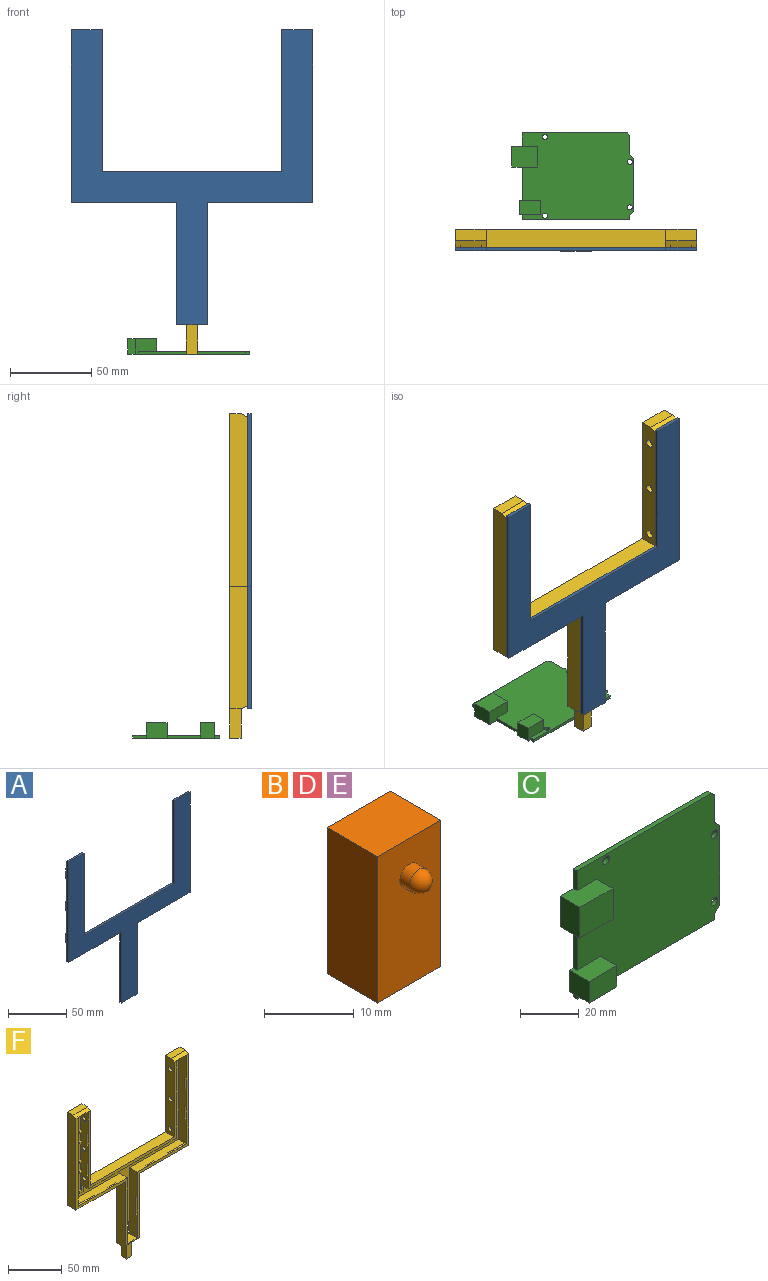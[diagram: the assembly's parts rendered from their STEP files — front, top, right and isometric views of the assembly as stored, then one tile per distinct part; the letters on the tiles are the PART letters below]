
ASSEMBLY  parts=6 mates=3
PART A: 170 faces, bbox 148x7x181 mm
  f0: plane 181x148mm, normal (0,1,0), area 6824.8mm2, adj f1,f2,f3,f4,f5,f6,f7,f11
  f1: plane 19x2mm, normal (0,0,-1), area 38mm2, adj f0,f7,f8,f84
  f2: plane 110x2mm, normal (0,0,1), area 220mm2, adj f0,f3,f8,f80
  f3: plane 87x2mm, normal (1,0,0), area 174mm2, adj f0,f2,f4,f8
  f4: plane 19x2mm, normal (0,0,1), area 38mm2, adj f0,f3,f5,f8
  f5: plane 106x2mm, normal (-1,0,0), area 212mm2, adj f0,f4,f6,f8
  f6: plane 64.5x2mm, normal (0,0,-1), area 129mm2, adj f0,f5,f7,f8
  f7: plane 75x2mm, normal (-1,0,0), area 150mm2, adj f0,f1,f6,f8
  f8: plane 181x148mm, normal (0,-1,0), area 7543mm2, adj f1,f2,f3,f4,f5,f6,f7,f80
  f9: plane 11.93x0.86mm, normal (0.71,0.71,0), area 14.2mm2, adj f10,f13,f14,f15
  f10: plane 13x2mm, normal (0,1,0), area 24.9mm2, adj f9,f11,f14,f15
  f11: plane 13x1.86mm, normal (-1,0,0), area 24.2mm2, adj f0,f10,f14,f15
  f12: plane 11.93x0.14mm, normal (1,0,0), area 1.7mm2, adj f0,f13,f14,f15
  f13: plane 11.93x0.86mm, normal (0.71,-0.71,0), area 14.2mm2, adj f9,f12,f14,f15
  f14: plane 2.86x1.86mm, normal (0.26,0,-0.97), area 4.6mm2, adj f0,f9,f10,f11,f12,f13
  f15: plane 2.86x1.86mm, normal (0.26,0,0.97), area 4.6mm2, adj f0,f9,f10,f11,f12,f13
  f16: plane 11.93x0.86mm, normal (-0.71,-0.71,0), area 14.2mm2, adj f17,f20,f21,f22
  f17: plane 11.93x0.14mm, normal (-1,0,0), area 1.7mm2, adj f0,f16,f21,f22
  f18: plane 13x1.86mm, normal (1,0,0), area 24.2mm2, adj f0,f19,f21,f22
  f19: plane 13x2mm, normal (0,1,0), area 24.9mm2, adj f18,f20,f21,f22
  f20: plane 11.93x0.86mm, normal (-0.71,0.71,0), area 14.2mm2, adj f16,f19,f21,f22
  f21: plane 2.86x1.86mm, normal (-0.26,0,-0.97), area 4.6mm2, adj f0,f16,f17,f18,f19,f20
  f22: plane 2.86x1.86mm, normal (-0.26,0,0.97), area 4.6mm2, adj f0,f16,f17,f18,f19,f20
  f23: plane 11.93x0.86mm, normal (0.71,0.71,0), area 14.2mm2, adj f24,f27,f28,f29
  f24: plane 13x2mm, normal (0,1,0), area 24.9mm2, adj f23,f25,f28,f29
  f25: plane 13x1.86mm, normal (-1,0,0), area 24.2mm2, adj f0,f24,f28,f29
  f26: plane 11.93x0.14mm, normal (1,0,0), area 1.7mm2, adj f0,f27,f28,f29
  f27: plane 11.93x0.86mm, normal (0.71,-0.71,0), area 14.2mm2, adj f23,f26,f28,f29
  f28: plane 2.86x1.86mm, normal (0.26,0,-0.97), area 4.6mm2, adj f0,f23,f24,f25,f26,f27
  f29: plane 2.86x1.86mm, normal (0.26,0,0.97), area 4.6mm2, adj f0,f23,f24,f25,f26,f27
  f30: plane 11.93x0.86mm, normal (-0.71,-0.71,0), area 14.2mm2, adj f31,f34,f35,f36
  f31: plane 11.93x0.14mm, normal (-1,0,0), area 1.7mm2, adj f0,f30,f35,f36
  f32: plane 13x1.86mm, normal (1,0,0), area 24.2mm2, adj f0,f33,f35,f36
  f33: plane 13x2mm, normal (0,1,0), area 24.9mm2, adj f32,f34,f35,f36
  f34: plane 11.93x0.86mm, normal (-0.71,0.71,0), area 14.2mm2, adj f30,f33,f35,f36
  f35: plane 2.86x1.86mm, normal (-0.26,0,-0.97), area 4.6mm2, adj f0,f30,f31,f32,f33,f34
  f36: plane 2.86x1.86mm, normal (-0.26,0,0.97), area 4.6mm2, adj f0,f30,f31,f32,f33,f34
  f37: plane 8.93x0.86mm, normal (0,-0.71,0.71), area 10.6mm2, adj f38,f41,f42,f43
  f38: plane 8.93x0.14mm, normal (0,0,1), area 1.3mm2, adj f0,f37,f42,f43
  f39: plane 10x1.86mm, normal (0,0,-1), area 18.6mm2, adj f0,f40,f42,f43
  f40: plane 10x2mm, normal (0,1,0), area 18.9mm2, adj f39,f41,f42,f43
  f41: plane 8.93x0.86mm, normal (0,0.71,0.71), area 10.6mm2, adj f37,f40,f42,f43
  f42: plane 2.86x1.86mm, normal (0.97,0,0.26), area 4.6mm2, adj f0,f37,f38,f39,f40,f41
  f43: plane 2.86x1.86mm, normal (-0.97,0,0.26), area 4.6mm2, adj f0,f37,f38,f39,f40,f41
  f44: plane 8.93x0.86mm, normal (0,-0.71,-0.71), area 10.6mm2, adj f45,f48,f49,f50
  f45: plane 8.93x0.86mm, normal (0,0.71,-0.71), area 10.6mm2, adj f44,f46,f49,f50
  f46: plane 10x2mm, normal (0,1,0), area 18.9mm2, adj f45,f47,f49,f50
  f47: plane 10x1.86mm, normal (0,0,1), area 18.6mm2, adj f0,f46,f49,f50
  f48: plane 8.93x0.14mm, normal (0,0,-1), area 1.3mm2, adj f0,f44,f49,f50
  f49: plane 2.86x1.86mm, normal (0.97,0,-0.26), area 4.6mm2, adj f0,f44,f45,f46,f47,f48
  f50: plane 2.86x1.86mm, normal (-0.97,0,-0.26), area 4.6mm2, adj f0,f44,f45,f46,f47,f48
  f51: plane 2.86x1.86mm, normal (-0.97,0,0.26), area 4.6mm2, adj f0,f52,f53,f54,f55
  f52: plane 9x1mm, normal (0,-0.71,0.71), area 12.4mm2, adj f0,f51,f53,f56
  f53: plane 8.93x0.86mm, normal (0,0.71,0.71), area 10.6mm2, adj f51,f52,f54,f56
  f54: plane 10x2mm, normal (0,1,0), area 18.9mm2, adj f51,f53,f55,f56
  f55: plane 10x1.86mm, normal (0,0,-1), area 18.6mm2, adj f0,f51,f54,f56
  f56: plane 2.86x1.86mm, normal (0.97,0,0.26), area 4.6mm2, adj f0,f52,f53,f54,f55
  f57: plane 21.93x1.86mm, normal (0,0,-1), area 40.8mm2, adj f0,f59,f60,f61
  f58: plane 23x1.86mm, normal (0,0,1), area 42.7mm2, adj f0,f59,f60,f61
  f59: plane 23x2mm, normal (0,1,0), area 44.9mm2, adj f57,f58,f60,f61
  f60: plane 2x1.86mm, normal (0.97,0,-0.26), area 3.8mm2, adj f0,f57,f58,f59
  f61: plane 2x1.86mm, normal (-0.97,0,-0.26), area 3.8mm2, adj f0,f57,f58,f59
  f62: plane 5x4mm, normal (0,0,1), area 16.9mm2, adj f0,f63,f65,f66,f77
  f63: plane 10x2.5mm, normal (1,0,0), area 25mm2, adj f0,f62,f64,f77
  f64: plane 5x4mm, normal (0,0,-1), area 16.9mm2, adj f0,f63,f65,f66,f77
  f65: plane 10x5mm, normal (-1,0,0), area 50mm2, adj f0,f62,f64,f66
  f66: plane 10x1.5mm, normal (0,1,0), area 15mm2, adj f62,f64,f65,f77
  f67: plane 5x4mm, normal (0,0,1), area 16.9mm2, adj f0,f68,f70,f71,f78
  f68: plane 10x2.5mm, normal (1,0,0), area 25mm2, adj f0,f67,f69,f78
  f69: plane 5x4mm, normal (0,0,-1), area 16.9mm2, adj f0,f68,f70,f71,f78
  f70: plane 10x5mm, normal (-1,0,0), area 50mm2, adj f0,f67,f69,f71
  f71: plane 10x1.5mm, normal (0,1,0), area 15mm2, adj f67,f69,f70,f78
  f72: plane 5x4mm, normal (0,0,1), area 16.9mm2, adj f0,f73,f75,f76,f79
  f73: plane 10x2.5mm, normal (1,0,0), area 25mm2, adj f0,f72,f74,f79
  f74: plane 5x4mm, normal (0,0,-1), area 16.9mm2, adj f0,f73,f75,f76,f79
  f75: plane 10x5mm, normal (-1,0,0), area 50mm2, adj f0,f72,f74,f76
  f76: plane 10x1.5mm, normal (0,1,0), area 15mm2, adj f72,f74,f75,f79
  f77: plane 10x2.5mm, normal (0.71,0.71,0), area 35.4mm2, adj f62,f63,f64,f66
  f78: plane 10x2.5mm, normal (0.71,0.71,0), area 35.4mm2, adj f67,f68,f69,f71
  f79: plane 10x2.5mm, normal (0.71,0.71,0), area 35.4mm2, adj f72,f73,f74,f76
  f80: plane 87x2mm, normal (-1,0,0), area 174mm2, adj f0,f2,f8,f81
  f81: plane 19x2mm, normal (0,0,1), area 38mm2, adj f0,f8,f80,f82
  f82: plane 106x2mm, normal (1,0,0), area 212mm2, adj f0,f8,f81,f83
  f83: plane 64.5x2mm, normal (0,0,-1), area 129mm2, adj f0,f8,f82,f84
  f84: plane 75x2mm, normal (1,0,0), area 150mm2, adj f0,f1,f8,f83
  f85: plane 11.93x0.86mm, normal (-0.71,0.71,0), area 14.2mm2, adj f86,f89,f90,f91
  f86: plane 13x2mm, normal (0,1,0), area 24.9mm2, adj f85,f87,f90,f91
  f87: plane 13x1.86mm, normal (1,0,0), area 24.2mm2, adj f0,f86,f90,f91
  f88: plane 11.93x0.14mm, normal (-1,0,0), area 1.7mm2, adj f0,f89,f90,f91
  f89: plane 11.93x0.86mm, normal (-0.71,-0.71,0), area 14.2mm2, adj f85,f88,f90,f91
  f90: plane 2.86x1.86mm, normal (-0.26,0,-0.97), area 4.6mm2, adj f0,f85,f86,f87,f88,f89
  f91: plane 2.86x1.86mm, normal (-0.26,0,0.97), area 4.6mm2, adj f0,f85,f86,f87,f88,f89
  f92: plane 11.93x0.86mm, normal (0.71,-0.71,0), area 14.2mm2, adj f93,f96,f97,f98
  f93: plane 11.93x0.14mm, normal (1,0,0), area 1.7mm2, adj f0,f92,f97,f98
  f94: plane 13x1.86mm, normal (-1,0,0), area 24.2mm2, adj f0,f95,f97,f98
  f95: plane 13x2mm, normal (0,1,0), area 24.9mm2, adj f94,f96,f97,f98
  f96: plane 11.93x0.86mm, normal (0.71,0.71,0), area 14.2mm2, adj f92,f95,f97,f98
  f97: plane 2.86x1.86mm, normal (0.26,0,-0.97), area 4.6mm2, adj f0,f92,f93,f94,f95,f96
  f98: plane 2.86x1.86mm, normal (0.26,0,0.97), area 4.6mm2, adj f0,f92,f93,f94,f95,f96
  f99: plane 11.93x0.86mm, normal (-0.71,0.71,0), area 14.2mm2, adj f100,f103,f104,f105
  f100: plane 13x2mm, normal (0,1,0), area 24.9mm2, adj f99,f101,f104,f105
  f101: plane 13x1.86mm, normal (1,0,0), area 24.2mm2, adj f0,f100,f104,f105
  f102: plane 11.93x0.14mm, normal (-1,0,0), area 1.7mm2, adj f0,f103,f104,f105
  f103: plane 11.93x0.86mm, normal (-0.71,-0.71,0), area 14.2mm2, adj f99,f102,f104,f105
  f104: plane 2.86x1.86mm, normal (-0.26,0,-0.97), area 4.6mm2, adj f0,f99,f100,f101,f102,f103
  f105: plane 2.86x1.86mm, normal (-0.26,0,0.97), area 4.6mm2, adj f0,f99,f100,f101,f102,f103
  f106: plane 11.93x0.86mm, normal (0.71,-0.71,0), area 14.2mm2, adj f107,f110,f111,f112
  f107: plane 11.93x0.14mm, normal (1,0,0), area 1.7mm2, adj f0,f106,f111,f112
  f108: plane 13x1.86mm, normal (-1,0,0), area 24.2mm2, adj f0,f109,f111,f112
  f109: plane 13x2mm, normal (0,1,0), area 24.9mm2, adj f108,f110,f111,f112
  f110: plane 11.93x0.86mm, normal (0.71,0.71,0), area 14.2mm2, adj f106,f109,f111,f112
  f111: plane 2.86x1.86mm, normal (0.26,0,-0.97), area 4.6mm2, adj f0,f106,f107,f108,f109,f110
  f112: plane 2.86x1.86mm, normal (0.26,0,0.97), area 4.6mm2, adj f0,f106,f107,f108,f109,f110
  f113: plane 8.93x0.86mm, normal (0,-0.71,0.71), area 10.6mm2, adj f114,f117,f118,f119
  f114: plane 8.93x0.14mm, normal (0,0,1), area 1.3mm2, adj f0,f113,f118,f119
  f115: plane 10x1.86mm, normal (0,0,-1), area 18.6mm2, adj f0,f116,f118,f119
  f116: plane 10x2mm, normal (0,1,0), area 18.9mm2, adj f115,f117,f118,f119
  f117: plane 8.93x0.86mm, normal (0,0.71,0.71), area 10.6mm2, adj f113,f116,f118,f119
  f118: plane 2.86x1.86mm, normal (-0.97,0,0.26), area 4.6mm2, adj f0,f113,f114,f115,f116,f117
  f119: plane 2.86x1.86mm, normal (0.97,0,0.26), area 4.6mm2, adj f0,f113,f114,f115,f116,f117
  f120: plane 8.93x0.86mm, normal (0,-0.71,-0.71), area 10.6mm2, adj f121,f124,f125,f126
  f121: plane 8.93x0.86mm, normal (0,0.71,-0.71), area 10.6mm2, adj f120,f122,f125,f126
  f122: plane 10x2mm, normal (0,1,0), area 18.9mm2, adj f121,f123,f125,f126
  f123: plane 10x1.86mm, normal (0,0,1), area 18.6mm2, adj f0,f122,f125,f126
  f124: plane 8.93x0.14mm, normal (0,0,-1), area 1.3mm2, adj f0,f120,f125,f126
  f125: plane 2.86x1.86mm, normal (-0.97,0,-0.26), area 4.6mm2, adj f0,f120,f121,f122,f123,f124
  f126: plane 2.86x1.86mm, normal (0.97,0,-0.26), area 4.6mm2, adj f0,f120,f121,f122,f123,f124
  f127: plane 2.86x1.86mm, normal (0.97,0,0.26), area 4.6mm2, adj f0,f128,f129,f130,f131
  f128: plane 9x1mm, normal (0,-0.71,0.71), area 12.4mm2, adj f0,f127,f129,f132
  f129: plane 8.93x0.86mm, normal (0,0.71,0.71), area 10.6mm2, adj f127,f128,f130,f132
  f130: plane 10x2mm, normal (0,1,0), area 18.9mm2, adj f127,f129,f131,f132
  f131: plane 10x1.86mm, normal (0,0,-1), area 18.6mm2, adj f0,f127,f130,f132
  f132: plane 2.86x1.86mm, normal (-0.97,0,0.26), area 4.6mm2, adj f0,f128,f129,f130,f131
  f133: plane 21.93x1.86mm, normal (0,0,-1), area 40.8mm2, adj f0,f135,f136,f137
  f134: plane 23x1.86mm, normal (0,0,1), area 42.7mm2, adj f0,f135,f136,f137
  f135: plane 23x2mm, normal (0,1,0), area 44.9mm2, adj f133,f134,f136,f137
  f136: plane 2x1.86mm, normal (-0.97,0,-0.26), area 3.8mm2, adj f0,f133,f134,f135
  f137: plane 2x1.86mm, normal (0.97,0,-0.26), area 3.8mm2, adj f0,f133,f134,f135
  f138: plane 5x4mm, normal (0,0,1), area 16.9mm2, adj f0,f139,f141,f142,f153
  f139: plane 10x2.5mm, normal (-1,0,0), area 25mm2, adj f0,f138,f140,f153
  f140: plane 5x4mm, normal (0,0,-1), area 16.9mm2, adj f0,f139,f141,f142,f153
  f141: plane 10x5mm, normal (1,0,0), area 50mm2, adj f0,f138,f140,f142
  f142: plane 10x1.5mm, normal (0,1,0), area 15mm2, adj f138,f140,f141,f153
  f143: plane 5x4mm, normal (0,0,1), area 16.9mm2, adj f0,f144,f146,f147,f154
  f144: plane 10x2.5mm, normal (-1,0,0), area 25mm2, adj f0,f143,f145,f154
  f145: plane 5x4mm, normal (0,0,-1), area 16.9mm2, adj f0,f144,f146,f147,f154
  f146: plane 10x5mm, normal (1,0,0), area 50mm2, adj f0,f143,f145,f147
  f147: plane 10x1.5mm, normal (0,1,0), area 15mm2, adj f143,f145,f146,f154
  f148: plane 5x4mm, normal (0,0,1), area 16.9mm2, adj f0,f149,f151,f152,f155
  f149: plane 10x2.5mm, normal (-1,0,0), area 25mm2, adj f0,f148,f150,f155
  f150: plane 5x4mm, normal (0,0,-1), area 16.9mm2, adj f0,f149,f151,f152,f155
  f151: plane 10x5mm, normal (1,0,0), area 50mm2, adj f0,f148,f150,f152
  f152: plane 10x1.5mm, normal (0,1,0), area 15mm2, adj f148,f150,f151,f155
  f153: plane 10x2.5mm, normal (-0.71,0.71,0), area 35.4mm2, adj f138,f139,f140,f142
  f154: plane 10x2.5mm, normal (-0.71,0.71,0), area 35.4mm2, adj f143,f144,f145,f147
  f155: plane 10x2.5mm, normal (-0.71,0.71,0), area 35.4mm2, adj f148,f149,f150,f152
  f156: plane 18.93x0.86mm, normal (-0.71,-0.71,0), area 22.7mm2, adj f157,f160,f161,f162
  f157: plane 18.93x0.14mm, normal (-1,0,0), area 2.7mm2, adj f0,f156,f161,f162
  f158: plane 20x1.86mm, normal (1,0,0), area 37.2mm2, adj f0,f159,f161,f162
  f159: plane 20x2mm, normal (0,1,0), area 38.9mm2, adj f158,f160,f161,f162
  f160: plane 18.93x0.86mm, normal (-0.71,0.71,0), area 22.7mm2, adj f156,f159,f161,f162
  f161: plane 2.86x1.86mm, normal (-0.26,0,0.97), area 4.6mm2, adj f0,f156,f157,f158,f159,f160
  f162: plane 2.86x1.86mm, normal (-0.26,0,-0.97), area 4.6mm2, adj f0,f156,f157,f158,f159,f160
  f163: plane 18.93x0.86mm, normal (0.71,0.71,0), area 22.7mm2, adj f164,f167,f168,f169
  f164: plane 20x2mm, normal (0,1,0), area 38.9mm2, adj f163,f165,f168,f169
  f165: plane 20x1.86mm, normal (-1,0,0), area 37.2mm2, adj f0,f164,f168,f169
  f166: plane 18.93x0.14mm, normal (1,0,0), area 2.7mm2, adj f0,f167,f168,f169
  f167: plane 18.93x0.86mm, normal (0.71,-0.71,0), area 22.7mm2, adj f163,f166,f168,f169
  f168: plane 2.86x1.86mm, normal (0.26,0,0.97), area 4.6mm2, adj f0,f163,f164,f165,f166,f167
  f169: plane 2.86x1.86mm, normal (0.26,0,-0.97), area 4.6mm2, adj f0,f163,f164,f165,f166,f167
PART B: 8 faces, bbox 10x11x20 mm
  f0: plane 10x8mm, normal (0,0,1), area 80mm2, adj f1,f3,f4,f5
  f1: plane 20x8mm, normal (-1,0,0), area 160mm2, adj f0,f2,f4,f5
  f2: plane 10x8mm, normal (0,0,-1), area 80mm2, adj f1,f3,f4,f5
  f3: plane 20x8mm, normal (1,0,0), area 160mm2, adj f0,f2,f4,f5
  f4: plane 20x10mm, normal (0,-1,0), area 192.9mm2, adj f0,f1,f2,f3,f6
  f5: plane 20x10mm, normal (0,1,0), area 200mm2, adj f0,f1,f2,f3
  f6: cylinder r=1.5mm len=3mm, axis (0,1,0), area 14.1mm2, adj f4,f7
  f7: sphere r=1.5mm, area 14.1mm2, adj f6
PART C: 27 faces, bbox 74.9x9.5x53.3 mm
  f0: plane 20.32x1.78mm, normal (-1,0,0), area 36.1mm2, adj f3,f16,f17,f23
  f1: plane 3.18x1.78mm, normal (-1,0,0), area 5.6mm2, adj f3,f6,f16,f22
  f2: plane 8.26x1.78mm, normal (-1,0,0), area 14.7mm2, adj f3,f5,f16,f18
  f3: plane 68.58x53.34mm, normal (0,-1,0), area 3356.8mm2, adj f0,f1,f2,f4,f5,f6,f7,f8
  f4: plane 1.78x1.52mm, normal (0.71,0,0.71), area 3.8mm2, adj f3,f5,f15,f16
  f5: plane 64.52x1.78mm, normal (0,0,1), area 114.7mm2, adj f2,f3,f4,f16
  f6: plane 66.04x1.78mm, normal (0,0,-1), area 117.4mm2, adj f1,f3,f7,f16
  f7: plane 2.54x1.78mm, normal (1,0,0), area 4.5mm2, adj f3,f6,f8,f16
  f8: plane 2.54x2.54mm, normal (0.71,0,-0.71), area 6.4mm2, adj f3,f7,f9,f16
  f9: plane 32.77x1.78mm, normal (1,0,0), area 58.3mm2, adj f3,f8,f10,f16
  f10: plane 2.54x2.54mm, normal (0.71,0,0.71), area 6.4mm2, adj f3,f9,f15,f16
  f11: cylinder r=1.59mm len=3.18mm, axis (0,1,0), area 17.7mm2, adj f3,f16
  f12: cylinder r=1.59mm len=3.18mm, axis (0,1,0), area 17.7mm2, adj f3,f16
  f13: cylinder r=1.59mm len=3.18mm, axis (0,1,0), area 17.7mm2, adj f3,f16
  f14: cylinder r=1.59mm len=3.18mm, axis (0,1,0), area 17.7mm2, adj f3,f16
  f15: plane 11.43x1.78mm, normal (1,0,0), area 20.3mm2, adj f3,f4,f10,f16
  f16: plane 74.93x53.34mm, normal (0,1,0), area 3677mm2, adj f0,f1,f2,f4,f5,f6,f7,f8
  f17: plane 15.88x9.53mm, normal (0,0,-1), area 134.3mm2, adj f0,f3,f16,f19,f20,f21
  f18: plane 15.88x9.53mm, normal (0,0,1), area 134.3mm2, adj f2,f3,f16,f19,f20,f21
  f19: plane 12.7x9.53mm, normal (-1,0,0), area 121mm2, adj f16,f17,f18,f21
  f20: plane 12.7x7.75mm, normal (1,0,0), area 98.4mm2, adj f3,f17,f18,f21
  f21: plane 15.88x12.7mm, normal (0,-1,0), area 201.6mm2, adj f17,f18,f19,f20
  f22: plane 13.34x9.53mm, normal (0,0,-1), area 106.7mm2, adj f1,f3,f16,f24,f25,f26
  f23: plane 13.34x9.53mm, normal (0,0,1), area 106.7mm2, adj f0,f3,f16,f24,f25,f26
  f24: plane 8.89x7.75mm, normal (1,0,0), area 68.9mm2, adj f3,f22,f23,f26
  f25: plane 9.53x8.89mm, normal (-1,0,0), area 84.7mm2, adj f16,f22,f23,f26
  f26: plane 13.34x8.89mm, normal (0,-1,0), area 118.5mm2, adj f22,f23,f24,f25
PART D: same geometry as B
PART E: same geometry as B
PART F: 152 faces, bbox 148x11.3x199 mm
  f0: plane 162x142mm, normal (0,-1,0), area 4853.4mm2, adj f2,f3,f4,f5,f6,f8,f10,f22
  f1: plane 177x148mm, normal (0,-1,0), area 1462mm2, adj f2,f3,f4,f6,f9,f14,f15,f16
  f2: plane 75x11.25mm, normal (1,0,0), area 742.7mm2, adj f0,f1,f4,f7,f9,f140,f142,f143
  f3: plane 75x11.25mm, normal (-1,0,0), area 742.7mm2, adj f0,f1,f7,f9,f73,f137,f138,f139
  f4: plane 64.5x10.25mm, normal (0,0,1), area 595.1mm2, adj f0,f1,f2,f6,f62,f64,f70,f71
  f5: plane 93.85x10.25mm, normal (-1,0,0), area 785.8mm2, adj f0,f8,f10,f18,f19,f20,f21,f22
  f6: plane 102x10.25mm, normal (1,0,0), area 984.2mm2, adj f0,f1,f4,f8,f44,f45,f46,f56
  f7: plane 199x148mm, normal (0,1,0), area 7488.3mm2, adj f2,f3,f9,f11,f12,f13,f14,f15
  f8: plane 13x10.25mm, normal (0,0,-1), area 133.2mm2, adj f0,f5,f6,f145
  f9: plane 13x11.25mm, normal (0,0,1), area 146.2mm2, adj f1,f2,f3,f7
  f10: plane 116x10.25mm, normal (0,0,-1), area 1103mm2, adj f0,f5,f18,f38,f42,f59,f61,f65
  f11: plane 110x11.25mm, normal (0,0,1), area 1237.5mm2, adj f7,f12,f18,f77
  f12: plane 87x11.25mm, normal (1,0,0), area 915.8mm2, adj f7,f11,f13,f18,f19,f20,f21,f145
  f13: plane 19x7.25mm, normal (0,0,1), area 137.7mm2, adj f7,f12,f14,f145
  f14: plane 106x11.25mm, normal (-1,0,0), area 1188.5mm2, adj f1,f7,f13,f15,f145
  f15: plane 64.5x11.25mm, normal (0,0,-1), area 725.6mm2, adj f1,f7,f14,f16
  f16: plane 75x11.25mm, normal (-1,0,0), area 839.8mm2, adj f1,f7,f15,f17,f146
  f17: plane 19x7.25mm, normal (0,0,-1), area 87.7mm2, adj f7,f16,f81,f146,f147,f148,f149
  f18: plane 116x88mm, normal (0,-1,0), area 858mm2, adj f5,f10,f11,f12,f48,f52,f60,f66
  f19: cylinder r=2.5mm len=5mm, axis (-1,0,0), area 47.1mm2, adj f5,f12
  f20: cylinder r=2.5mm len=5mm, axis (-1,0,0), area 47.1mm2, adj f5,f12
  f21: cylinder r=2.5mm len=5mm, axis (-1,0,0), area 47.1mm2, adj f5,f12
  f22: plane 2.5x2mm, normal (0,0,1), area 5mm2, adj f0,f5,f23,f25
  f23: plane 2x2mm, normal (-1,0,0), area 4mm2, adj f0,f22,f24,f25
  f24: plane 2.5x2mm, normal (0,0,-1), area 5mm2, adj f0,f5,f23,f25
  f25: plane 2.5x2mm, normal (0,-1,0), area 5mm2, adj f5,f22,f23,f24
  f26: plane 2.5x2mm, normal (0,0,1), area 5mm2, adj f0,f5,f27,f29
  f27: plane 2x2mm, normal (-1,0,0), area 4mm2, adj f0,f26,f28,f29
  f28: plane 2.5x2mm, normal (0,0,-1), area 5mm2, adj f0,f5,f27,f29
  f29: plane 2.5x2mm, normal (0,-1,0), area 5mm2, adj f5,f26,f27,f28
  f30: plane 2.5x2mm, normal (0,0,-1), area 5mm2, adj f0,f5,f32,f33
  f31: plane 2.5x2mm, normal (0,0,1), area 5mm2, adj f0,f5,f32,f33
  f32: plane 2x2mm, normal (-1,0,0), area 4mm2, adj f0,f30,f31,f33
  f33: plane 2.5x2mm, normal (0,-1,0), area 5mm2, adj f5,f30,f31,f32
  f34: plane 2.5x2mm, normal (0,0,-1), area 5mm2, adj f0,f5,f36,f37
  f35: plane 2.5x2mm, normal (0,0,1), area 5mm2, adj f0,f5,f36,f37
  f36: plane 2x2mm, normal (-1,0,0), area 4mm2, adj f0,f34,f35,f37
  f37: plane 2.5x2mm, normal (0,-1,0), area 5mm2, adj f5,f34,f35,f36
  f38: plane 7.85x2mm, normal (1,0,0), area 15.7mm2, adj f0,f10,f41,f42
  f39: plane 2.5x2mm, normal (0,0,1), area 5mm2, adj f0,f5,f40,f42
  f40: plane 2x2mm, normal (-1,0,0), area 4mm2, adj f0,f39,f41,f42
  f41: plane 4x2mm, normal (0,0,-1), area 8mm2, adj f0,f38,f40,f42
  f42: plane 7.85x4mm, normal (0,-1,0), area 16.8mm2, adj f5,f10,f38,f39,f40,f41
  f43: plane 13x1mm, normal (0.71,0.71,0), area 18.4mm2, adj f1,f44,f45,f46
  f44: plane 13x1mm, normal (0.71,-0.71,0), area 18.4mm2, adj f6,f43,f45,f46
  f45: plane 2x1mm, normal (0,0,1), area 1mm2, adj f6,f43,f44
  f46: plane 2x1mm, normal (0,0,-1), area 1mm2, adj f6,f43,f44
  f47: plane 13x1mm, normal (-0.71,-0.71,0), area 18.4mm2, adj f5,f48,f49,f50
  f48: plane 13x1mm, normal (-0.71,0.71,0), area 18.4mm2, adj f18,f47,f49,f50
  f49: plane 2x1mm, normal (0,0,1), area 1mm2, adj f5,f47,f48
  f50: plane 2x1mm, normal (0,0,-1), area 1mm2, adj f5,f47,f48
  f51: plane 13x1mm, normal (-0.71,-0.71,0), area 18.4mm2, adj f5,f52,f53,f54
  f52: plane 13x1mm, normal (-0.71,0.71,0), area 18.4mm2, adj f18,f51,f53,f54
  f53: plane 2x1mm, normal (0,0,1), area 1mm2, adj f5,f51,f52
  f54: plane 2x1mm, normal (0,0,-1), area 1mm2, adj f5,f51,f52
  f55: plane 13x1mm, normal (0.71,0.71,0), area 18.4mm2, adj f1,f56,f57,f58
  f56: plane 13x1mm, normal (0.71,-0.71,0), area 18.4mm2, adj f6,f55,f57,f58
  f57: plane 2x1mm, normal (0,0,1), area 1mm2, adj f6,f55,f56
  f58: plane 2x1mm, normal (0,0,-1), area 1mm2, adj f6,f55,f56
  f59: plane 10x1mm, normal (0,-0.71,-0.71), area 14.1mm2, adj f5,f10,f60,f61
  f60: plane 10x1mm, normal (0,0.71,-0.71), area 14.1mm2, adj f5,f18,f59,f61
  f61: plane 2x1mm, normal (-1,0,0), area 1mm2, adj f10,f59,f60
  f62: plane 2x1mm, normal (-1,0,0), area 1mm2, adj f4,f63,f64
  f63: plane 23x1mm, normal (0,0.71,0.71), area 32.5mm2, adj f1,f6,f62,f64
  f64: plane 23x1mm, normal (0,-0.71,0.71), area 32.5mm2, adj f4,f6,f62,f63
  f65: plane 10x1mm, normal (0,-0.71,-0.71), area 14.1mm2, adj f10,f66,f67,f68
  f66: plane 10x1mm, normal (0,0.71,-0.71), area 14.1mm2, adj f18,f65,f67,f68
  f67: plane 2x1mm, normal (-1,0,0), area 1mm2, adj f10,f65,f66
  f68: plane 2x1mm, normal (1,0,0), area 1mm2, adj f10,f65,f66
  f69: plane 10x1mm, normal (0,0.71,0.71), area 14.1mm2, adj f1,f70,f71,f72
  f70: plane 10x1mm, normal (0,-0.71,0.71), area 14.1mm2, adj f4,f69,f71,f72
  f71: plane 2x1mm, normal (-1,0,0), area 1mm2, adj f4,f69,f70
  f72: plane 2x1mm, normal (1,0,0), area 1mm2, adj f4,f69,f70
  f73: plane 64.5x10.25mm, normal (0,0,1), area 595.1mm2, adj f0,f1,f3,f75,f125,f127,f133,f134
  f74: plane 93.85x10.25mm, normal (1,0,0), area 785.8mm2, adj f0,f10,f18,f76,f82,f83,f84,f85
  f75: plane 102x10.25mm, normal (-1,0,0), area 984.2mm2, adj f0,f1,f73,f76,f107,f108,f109,f119
  f76: plane 13x10.25mm, normal (0,0,-1), area 133.2mm2, adj f0,f74,f75,f144
  f77: plane 87x11.25mm, normal (-1,0,0), area 915.8mm2, adj f7,f11,f18,f78,f82,f83,f84,f144
  f78: plane 19x7.25mm, normal (0,0,1), area 137.7mm2, adj f7,f77,f79,f144
  f79: plane 106x11.25mm, normal (1,0,0), area 1188.5mm2, adj f1,f7,f78,f80,f144
  f80: plane 64.5x11.25mm, normal (0,0,-1), area 725.6mm2, adj f1,f7,f79,f81
  f81: plane 75x11.25mm, normal (1,0,0), area 839.8mm2, adj f1,f7,f17,f80,f146
  f82: cylinder r=2.5mm len=5mm, axis (1,0,0), area 47.1mm2, adj f74,f77
  f83: cylinder r=2.5mm len=5mm, axis (1,0,0), area 47.1mm2, adj f74,f77
  f84: cylinder r=2.5mm len=5mm, axis (1,0,0), area 47.1mm2, adj f74,f77
  f85: plane 2.5x2mm, normal (0,0,1), area 5mm2, adj f0,f74,f86,f88
  f86: plane 2x2mm, normal (1,0,0), area 4mm2, adj f0,f85,f87,f88
  f87: plane 2.5x2mm, normal (0,0,-1), area 5mm2, adj f0,f74,f86,f88
  f88: plane 2.5x2mm, normal (0,-1,0), area 5mm2, adj f74,f85,f86,f87
  f89: plane 2.5x2mm, normal (0,0,1), area 5mm2, adj f0,f74,f90,f92
  f90: plane 2x2mm, normal (1,0,0), area 4mm2, adj f0,f89,f91,f92
  f91: plane 2.5x2mm, normal (0,0,-1), area 5mm2, adj f0,f74,f90,f92
  f92: plane 2.5x2mm, normal (0,-1,0), area 5mm2, adj f74,f89,f90,f91
  f93: plane 2.5x2mm, normal (0,0,-1), area 5mm2, adj f0,f74,f95,f96
  f94: plane 2.5x2mm, normal (0,0,1), area 5mm2, adj f0,f74,f95,f96
  f95: plane 2x2mm, normal (1,0,0), area 4mm2, adj f0,f93,f94,f96
  f96: plane 2.5x2mm, normal (0,-1,0), area 5mm2, adj f74,f93,f94,f95
  f97: plane 2.5x2mm, normal (0,0,-1), area 5mm2, adj f0,f74,f99,f100
  f98: plane 2.5x2mm, normal (0,0,1), area 5mm2, adj f0,f74,f99,f100
  f99: plane 2x2mm, normal (1,0,0), area 4mm2, adj f0,f97,f98,f100
  f100: plane 2.5x2mm, normal (0,-1,0), area 5mm2, adj f74,f97,f98,f99
  f101: plane 7.85x2mm, normal (-1,0,0), area 15.7mm2, adj f0,f10,f104,f105
  f102: plane 2.5x2mm, normal (0,0,1), area 5mm2, adj f0,f74,f103,f105
  f103: plane 2x2mm, normal (1,0,0), area 4mm2, adj f0,f102,f104,f105
  f104: plane 4x2mm, normal (0,0,-1), area 8mm2, adj f0,f101,f103,f105
  f105: plane 7.85x4mm, normal (0,-1,0), area 16.8mm2, adj f10,f74,f101,f102,f103,f104
  f106: plane 13x1mm, normal (-0.71,0.71,0), area 18.4mm2, adj f1,f107,f108,f109
  f107: plane 13x1mm, normal (-0.71,-0.71,0), area 18.4mm2, adj f75,f106,f108,f109
  f108: plane 2x1mm, normal (0,0,1), area 1mm2, adj f75,f106,f107
  f109: plane 2x1mm, normal (0,0,-1), area 1mm2, adj f75,f106,f107
  f110: plane 13x1mm, normal (0.71,-0.71,0), area 18.4mm2, adj f74,f111,f112,f113
  f111: plane 13x1mm, normal (0.71,0.71,0), area 18.4mm2, adj f18,f110,f112,f113
  f112: plane 2x1mm, normal (0,0,1), area 1mm2, adj f74,f110,f111
  f113: plane 2x1mm, normal (0,0,-1), area 1mm2, adj f74,f110,f111
  f114: plane 13x1mm, normal (0.71,-0.71,0), area 18.4mm2, adj f74,f115,f116,f117
  f115: plane 13x1mm, normal (0.71,0.71,0), area 18.4mm2, adj f18,f114,f116,f117
  f116: plane 2x1mm, normal (0,0,1), area 1mm2, adj f74,f114,f115
  f117: plane 2x1mm, normal (0,0,-1), area 1mm2, adj f74,f114,f115
  f118: plane 13x1mm, normal (-0.71,0.71,0), area 18.4mm2, adj f1,f119,f120,f121
  f119: plane 13x1mm, normal (-0.71,-0.71,0), area 18.4mm2, adj f75,f118,f120,f121
  f120: plane 2x1mm, normal (0,0,1), area 1mm2, adj f75,f118,f119
  f121: plane 2x1mm, normal (0,0,-1), area 1mm2, adj f75,f118,f119
  f122: plane 10x1mm, normal (0,-0.71,-0.71), area 14.1mm2, adj f10,f74,f123,f124
  f123: plane 10x1mm, normal (0,0.71,-0.71), area 14.1mm2, adj f18,f74,f122,f124
  f124: plane 2x1mm, normal (1,0,0), area 1mm2, adj f10,f122,f123
  f125: plane 2x1mm, normal (1,0,0), area 1mm2, adj f73,f126,f127
  f126: plane 23x1mm, normal (0,0.71,0.71), area 32.5mm2, adj f1,f75,f125,f127
  f127: plane 23x1mm, normal (0,-0.71,0.71), area 32.5mm2, adj f73,f75,f125,f126
  f128: plane 10x1mm, normal (0,-0.71,-0.71), area 14.1mm2, adj f10,f129,f130,f131
  f129: plane 10x1mm, normal (0,0.71,-0.71), area 14.1mm2, adj f18,f128,f130,f131
  f130: plane 2x1mm, normal (1,0,0), area 1mm2, adj f10,f128,f129
  f131: plane 2x1mm, normal (-1,0,0), area 1mm2, adj f10,f128,f129
  f132: plane 10x1mm, normal (0,0.71,0.71), area 14.1mm2, adj f1,f133,f134,f135
  f133: plane 10x1mm, normal (0,-0.71,0.71), area 14.1mm2, adj f73,f132,f134,f135
  f134: plane 2x1mm, normal (1,0,0), area 1mm2, adj f73,f132,f133
  f135: plane 2x1mm, normal (-1,0,0), area 1mm2, adj f73,f132,f133
  f136: plane 20x1mm, normal (-0.71,0.71,0), area 28.3mm2, adj f1,f137,f138,f139
  f137: plane 20x1mm, normal (-0.71,-0.71,0), area 28.3mm2, adj f3,f136,f138,f139
  f138: plane 2x1mm, normal (0,0,1), area 1mm2, adj f3,f136,f137
  f139: plane 2x1mm, normal (0,0,-1), area 1mm2, adj f3,f136,f137
  f140: plane 20x1mm, normal (0.71,-0.71,0), area 28.3mm2, adj f2,f141,f142,f143
  f141: plane 20x1mm, normal (0.71,0.71,0), area 28.3mm2, adj f1,f140,f142,f143
  f142: plane 2x1mm, normal (0,0,1), area 1mm2, adj f2,f140,f141
  f143: plane 2x1mm, normal (0,0,-1), area 1mm2, adj f2,f140,f141
  f144: plane 19x4mm, normal (0,-0.45,0.89), area 85mm2, adj f1,f18,f76,f77,f78,f79
  f145: plane 19x4mm, normal (0,-0.45,0.89), area 85mm2, adj f1,f8,f12,f13,f14,f18
  f146: plane 19x4mm, normal (0,-0.45,-0.89), area 85mm2, adj f1,f16,f17,f81
  f147: plane 18x7.07mm, normal (-1,0,0), area 127.3mm2, adj f7,f17,f149,f150
  f148: plane 18x7.07mm, normal (1,0,0), area 127.3mm2, adj f7,f17,f149,f150
  f149: plane 18x7.07mm, normal (0,-1,0), area 127.3mm2, adj f17,f147,f148,f150
  f150: plane 7.07x7.07mm, normal (0,0,-1), area 50mm2, adj f7,f147,f148,f149
  f151: plane 13x1mm, normal (0,0,-1), area 13mm2, adj f0,f2,f3,f7
PLACE A t=(9.59,20.86,16.47)mm
PLACE B rot(axis=(0,0,1),90deg) t=(-56.41,14.73,72.97)mm
PLACE C rot(axis=(-1,0,0),90deg) t=(18.3,31.94,-40.53)mm
PLACE D rot(axis=(0,0,1),90deg) t=(-56.41,14.73,140.97)mm
PLACE E rot(axis=(0,0,1),90deg) t=(-56.41,14.73,106.97)mm
PLACE F t=(9.59,20.86,16.47)mm
MATE fastened F.f150 <-> C.f16  axis (0,0,-1) through (9.59,20.86,-40.53)mm
MATE fastened D.f4 <-> F.f5  axis (1,0,0) through (-48.41,14.73,150.97)mm
MATE fastened A.f0 <-> F.f1  axis (0,1,0) through (0.09,9.61,52.47)mm
